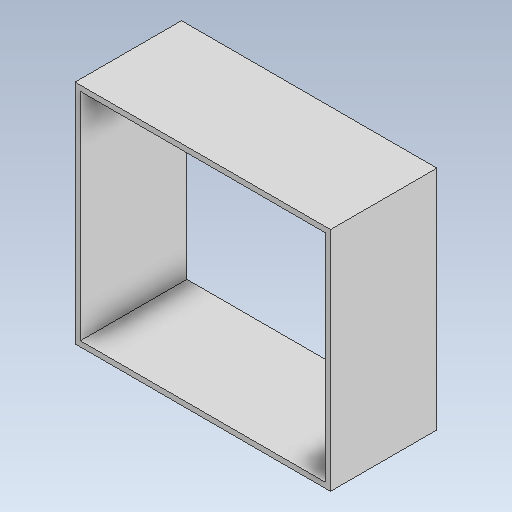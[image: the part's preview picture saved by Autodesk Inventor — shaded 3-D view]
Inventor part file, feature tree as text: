
AUTODESK INVENTOR PART (.ipt)
format: ipt  version: 2021 (Build 250183000, 183)  size: 101,376 bytes
history: native  units: mm
features: extrude x1, sketch x1
ambient origin geometry x8: Origin, YZ Plane, XZ Plane, XY Plane, X Axis, Y Axis, Z Axis, Center Point
bodies: Solid1 (feature_tree)
feature tree (2):
  extrude  "Extrusion1"  Depth=81.2mm
  sketch  "Sketch1"  dims[d0=92.0mm d1=81.2mm d2=40.6mm d3=40.6mm d4=2.0mm d5=2.0mm d6=2.0mm d7=2.0mm d8=40.0mm d9=0.0mm]
